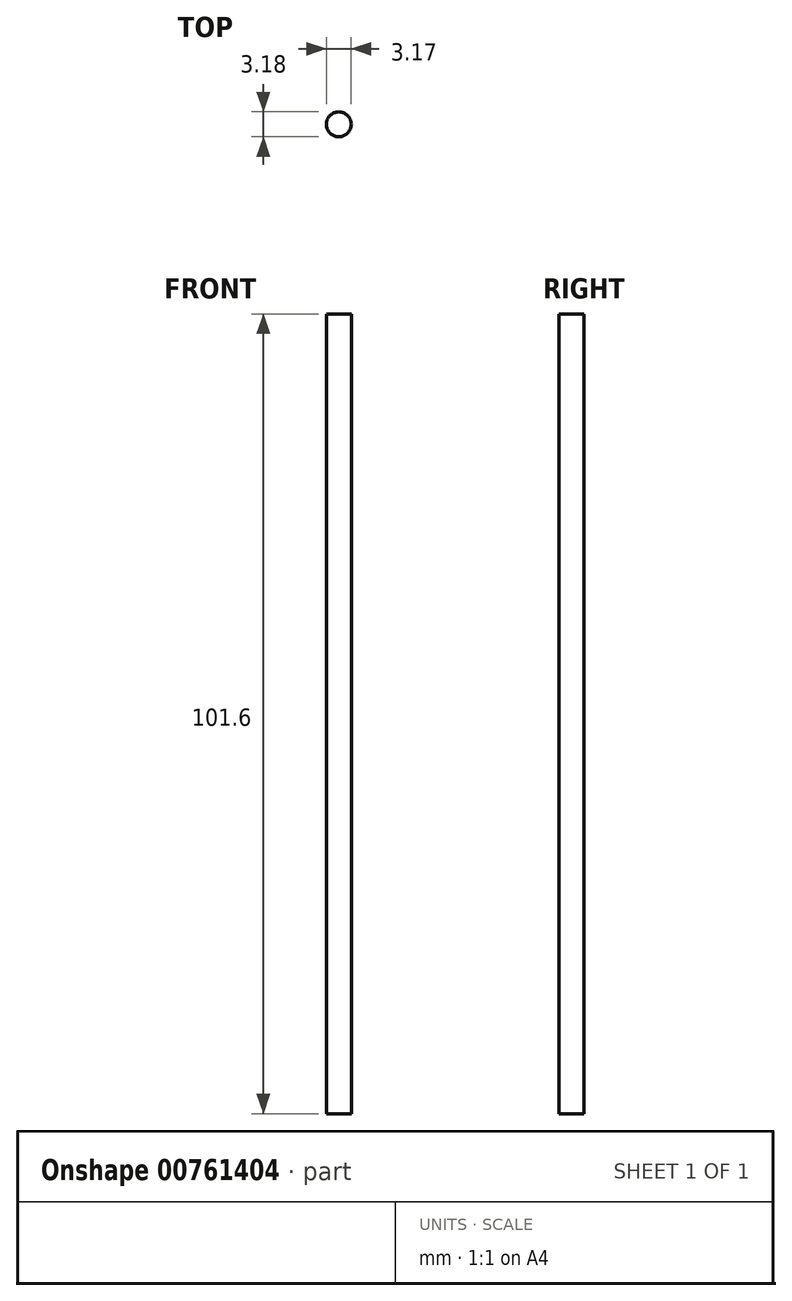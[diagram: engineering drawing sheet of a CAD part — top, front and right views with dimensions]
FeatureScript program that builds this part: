
annotation { "Feature Type Name" : "Feature", "Feature Type Description" : "" }
export const myFeature = defineFeature(function(context is Context, id is Id, definition is map)
    precondition{}
    {
        {
            var Q0;
            Q0=qCreatedBy(makeId("Top.planeOp"),FACE);
            var sketch = newSketch(context, id + "F0", { "sketchPlane" : qUnion([Q0])});
            skCircle(sketch, "E0", {"center": v(-10.44, 4.07) * mm, "radius": 1.59 * mm});
            skSolve(sketch);
        }
        {
            var Q0;
            Q0=makeQuery(id+"F0.imprint","IMPRINT",FACE,{"disambiguationData":[TD([[makeQuery(id+"F0.imprint","IMPRINT",EDGE,{"derivedFrom":sQuery(id+"F0.wireOp",EDGE,"E0")}),1.0]])]});
            extrude(context, id + "F1", {"entities" : qUnion([Q0]), "depth" : 101.6 * mm, "offsetDistance" : 25.4 * mm});
        }
    });
